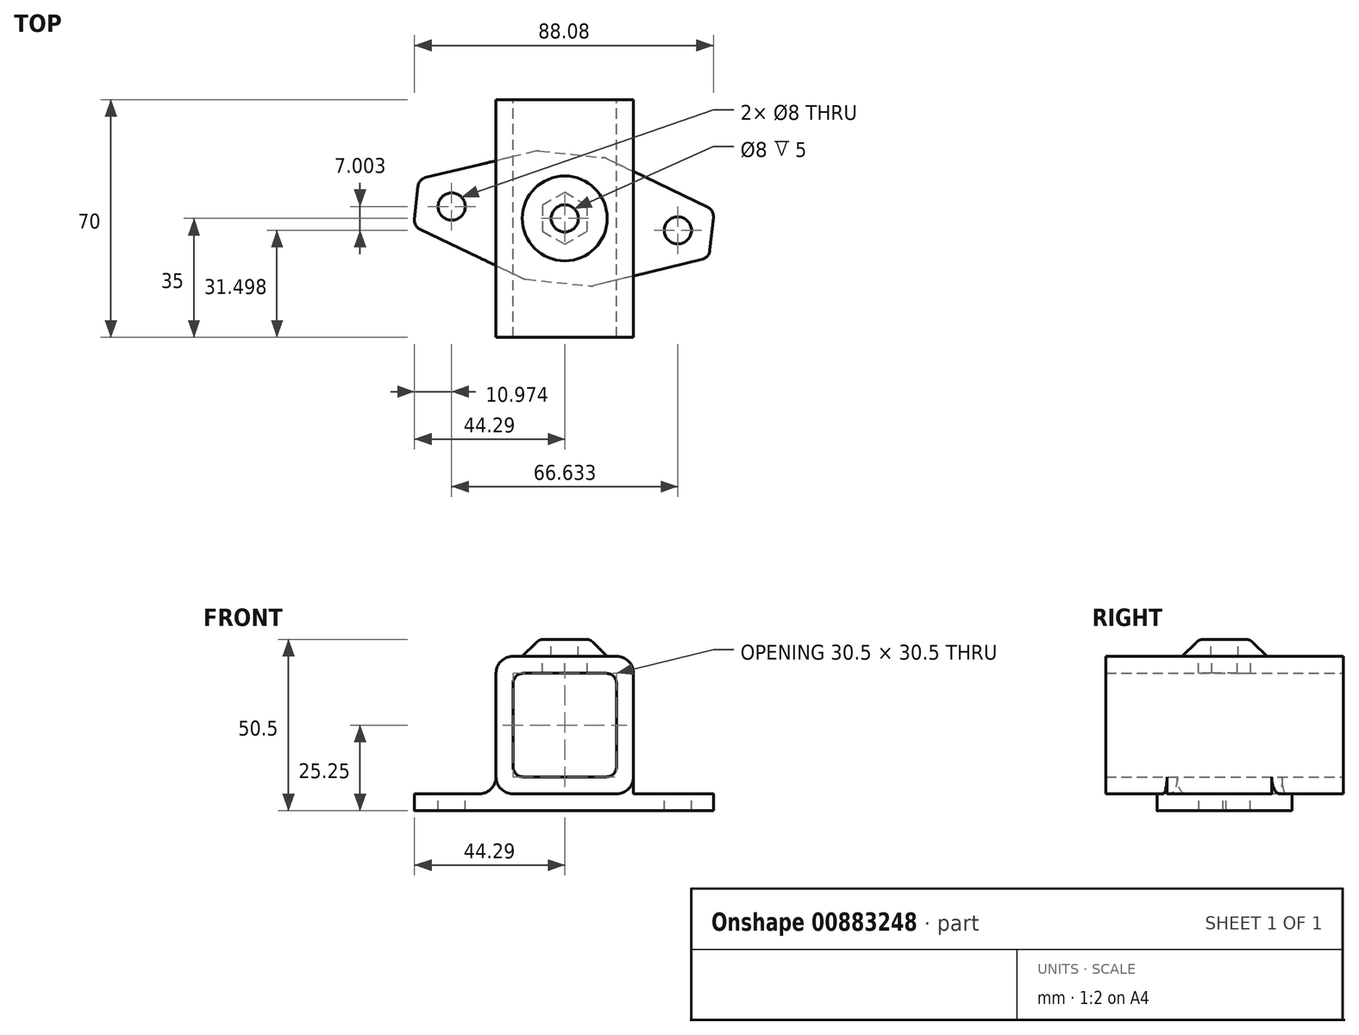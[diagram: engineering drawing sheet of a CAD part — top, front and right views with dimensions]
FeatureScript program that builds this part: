
annotation { "Feature Type Name" : "Feature", "Feature Type Description" : "" }
export const myFeature = defineFeature(function(context is Context, id is Id, definition is map)
    precondition{}
    {
        {
            var Q0;
            Q0=qCreatedBy(makeId("Front.planeOp"),FACE);
            var sketch = newSketch(context, id + "F0", { "sketchPlane" : qUnion([Q0])});
            skLineSegment(sketch, "E0.bottom", {"start": v(-12.25, -15.25) * mm, "end": v(12.25, -15.25) * mm});
            skLineSegment(sketch, "E0.top", {"start": v(-12.25, 15.25) * mm, "end": v(12.25, 15.25) * mm});
            skLineSegment(sketch, "E0.left", {"start": v(-15.25, -12.25) * mm, "end": v(-15.25, 12.25) * mm});
            skLineSegment(sketch, "E0.right", {"start": v(15.25, -12.25) * mm, "end": v(15.25, 12.25) * mm});
            skPoint(sketch, "E0.middle", {"position": v(0, 0) * mm});
            skLineSegment(sketch, "E1.0", {"start": v(-20.25, -20.25) * mm, "end": v(-20.25, 15.25) * mm});
            skLineSegment(sketch, "E1.1", {"start": v(-20.25, -20.25) * mm, "end": v(20.25, -20.25) * mm});
            skLineSegment(sketch, "E1.2", {"start": v(20.25, -20.25) * mm, "end": v(20.25, 15.25) * mm});
            skLineSegment(sketch, "E1.3", {"start": v(-15.25, 20.25) * mm, "end": v(15.25, 20.25) * mm});
            skPoint(sketch, "E2.visualSharp", {"position": v(-15.25, 15.25) * mm});
            skArc(sketch, "E2.filletArc", {"start": v(-12.25, 15.25) * mm, "mid": v(-14.37, 14.37) * mm, "end": v(-15.25, 12.25) * mm});
            skPoint(sketch, "E3.visualSharp", {"position": v(15.25, 15.25) * mm});
            skArc(sketch, "E3.filletArc", {"start": v(15.25, 12.25) * mm, "mid": v(14.37, 14.37) * mm, "end": v(12.25, 15.25) * mm});
            skPoint(sketch, "E4.visualSharp", {"position": v(15.25, -15.25) * mm});
            skArc(sketch, "E4.filletArc", {"start": v(12.25, -15.25) * mm, "mid": v(14.37, -14.37) * mm, "end": v(15.25, -12.25) * mm});
            skPoint(sketch, "E5.visualSharp", {"position": v(-15.25, -15.25) * mm});
            skArc(sketch, "E5.filletArc", {"start": v(-15.25, -12.25) * mm, "mid": v(-14.37, -14.37) * mm, "end": v(-12.25, -15.25) * mm});
            skPoint(sketch, "E6.visualSharp", {"position": v(-20.25, -20.25) * mm});
            skPoint(sketch, "E7.visualSharp", {"position": v(-20.25, 20.25) * mm});
            skArc(sketch, "E7.filletArc", {"start": v(-15.25, 20.25) * mm, "mid": v(-18.79, 18.79) * mm, "end": v(-20.25, 15.25) * mm});
            skPoint(sketch, "E8.visualSharp", {"position": v(20.25, 20.25) * mm});
            skArc(sketch, "E8.filletArc", {"start": v(20.25, 15.25) * mm, "mid": v(18.79, 18.79) * mm, "end": v(15.25, 20.25) * mm});
            skPoint(sketch, "E9.visualSharp", {"position": v(20.25, -20.25) * mm});
            skSolve(sketch);
        }
        {
            var Q0;
            Q0=makeQuery(id+"F0.imprint","IMPRINT",FACE,{"disambiguationData":[TD([[makeQuery(id+"F0.imprint","IMPRINT",EDGE,{"derivedFrom":sQuery(id+"F0.wireOp",EDGE,"E0.bottom")}),-1.0]])]});
            extrude(context, id + "F1", {"entities" : qUnion([Q0]), "endBound" : BoundingType.SYMMETRIC, "depth" : 70 * mm, "offsetDistance" : 25 * mm});
        }
        {
            var Q0;
            Q0=makeQuery(id+"F1.opExtrude","SWEPT_FACE",FACE,{"disambiguationData":[OSD([sQuery(id+"F0.wireOp",EDGE,"E1.3")])]});
            var sketch = newSketch(context, id + "F2", { "sketchPlane" : qUnion([Q0])});
            skCircle(sketch, "E10.cCircle", {"center": v(0, 0) * mm, "radius": 6.6 * mm, "construction": true});
            skLineSegment(sketch, "E10.0", {"start": v(6.6, 3.81) * mm, "end": v(6.6, -3.81) * mm});
            skLineSegment(sketch, "E10.1", {"start": v(6.6, -3.81) * mm, "end": v(0, -7.62) * mm});
            skLineSegment(sketch, "E10.2", {"start": v(0, -7.62) * mm, "end": v(-6.6, -3.81) * mm});
            skLineSegment(sketch, "E10.3", {"start": v(-6.6, -3.81) * mm, "end": v(-6.6, 3.81) * mm});
            skLineSegment(sketch, "E10.4", {"start": v(-6.6, 3.81) * mm, "end": v(0, 7.62) * mm});
            skLineSegment(sketch, "E10.5", {"start": v(0, 7.62) * mm, "end": v(6.6, 3.81) * mm});
            skPoint(sketch, "E10.0.midPoint", {"position": v(6.6, 0) * mm});
            skSolve(sketch);
        }
        {
            var Q0;
            Q0 = qSketchRegion(id + "F2", true);
            extrude(context, id + "F3", {"entities" : qUnion([Q0]), "operationType" : NewBodyOperationType.REMOVE, "endBound" : BoundingType.UP_TO_NEXT, "oppositeDirection" : true, "depth" : 25 * mm, "offsetDistance" : 25 * mm});
        }
        {
            var Q0;
            Q0=makeQuery(id+"F1.opExtrude","SWEPT_FACE",FACE,{"disambiguationData":[OSD([sQuery(id+"F0.wireOp",EDGE,"E1.3")])]});
            var sketch = newSketch(context, id + "F4", { "sketchPlane" : qUnion([Q0])});
            skCircle(sketch, "E11", {"center": v(0, 0) * mm, "radius": 12.5 * mm});
            skSolve(sketch);
        }
        {
            var Q0;
            Q0=makeQuery(id+"F4.imprint","IMPRINT",FACE,{"disambiguationData":[TD([[makeQuery(id+"F4.imprint","IMPRINT",EDGE,{"derivedFrom":sQuery(id+"F4.wireOp",EDGE,"E11")}),-1.0]])]});
            cPlane(context, id + "F5", {"entities" : qUnion([Q0]), "cplaneType" : CPlaneType.OFFSET, "offset" : 5 * mm, "width" : 150 * mm, "height" : 150 * mm});
        }
        {
            var Q0;
            Q0=qCreatedBy(id+"F5.planeOp",FACE);
            var sketch = newSketch(context, id + "F6", { "sketchPlane" : qUnion([Q0])});
            skCircle(sketch, "E12", {"center": v(0, 0) * mm, "radius": 7.5 * mm});
            skSolve(sketch);
        }
        {
            var Q0;
            Q0=makeQuery(id+"F1.opExtrude","SWEPT_FACE",FACE,{"disambiguationData":[OSD([sQuery(id+"F0.wireOp",EDGE,"E1.3")])]});
            cPlane(context, id + "F7", {"entities" : qUnion([Q0]), "cplaneType" : CPlaneType.OFFSET, "offset" : 0 * mm, "width" : 150 * mm, "height" : 150 * mm});
        }
        {
            var Q0;
            Q0=qCreatedBy(id+"F7.planeOp",FACE);
            var sketch = newSketch(context, id + "F8", { "sketchPlane" : qUnion([Q0])});
            skCircle(sketch, "E13", {"center": v(0, 0) * mm, "radius": 12.5 * mm});
            skSolve(sketch);
        }
        {
            var Q1;
            Q1 = qSketchRegion(id + "F8", true);
            var Q2;
            Q2 = qSketchRegion(id + "F6", true);
            loft(context, id + "F9", {"operationType" : NewBodyOperationType.ADD, "sheetProfilesArray" : [{ "sheetProfileEntities" : qUnion([Q1]) }, { "sheetProfileEntities" : qUnion([Q2]) }]});
        }
        {
            var Q0;
            Q0=makeQuery(id+"F9.opLoft","MID_CAP_EDGE",EDGE,{"disambiguationData":[OSD([sQuery(id+"F8.wireOp",EDGE,"E13")])],"capPos":0.0});
            var Q1;
            Q1=makeQuery(id+"F9.opLoft","MID_CAP_EDGE",EDGE,{"disambiguationData":[OSD([sQuery(id+"F6.wireOp",EDGE,"E12")])],"capPos":1.0});
            fillet(context, id + "F10", {"entities" : qUnion([Q0, Q1]), "radius" : 3 * mm, "tangentPropagation" : true, "allowEdgeOverflow" : false});
        }
        {
            var Q0;
            Q0=makeQuery(id+"F6.imprint","IMPRINT",FACE,{"disambiguationData":[TD([[makeQuery(id+"F6.imprint","IMPRINT",EDGE,{"derivedFrom":sQuery(id+"F6.wireOp",EDGE,"E12")}),1.0]])]});
            var sketch = newSketch(context, id + "F11", { "sketchPlane" : qUnion([Q0])});
            skCircle(sketch, "E14", {"center": v(0, 0) * mm, "radius": 4 * mm});
            skSolve(sketch);
        }
        {
            var Q0;
            Q0 = qSketchRegion(id + "F11", true);
            extrude(context, id + "F12", {"entities" : qUnion([Q0]), "operationType" : NewBodyOperationType.REMOVE, "endBound" : BoundingType.UP_TO_NEXT, "oppositeDirection" : true, "depth" : 25 * mm, "offsetDistance" : 25 * mm});
        }
        {
            var Q0;
            Q0=makeQuery(id+"F1.opExtrude","SWEPT_FACE",FACE,{"disambiguationData":[OSD([sQuery(id+"F0.wireOp",EDGE,"E1.1")])]});
            var sketch = newSketch(context, id + "F13", { "sketchPlane" : qUnion([Q0])});
            skLineSegment(sketch, "E15", {"start": v(-33.32, -3.5) * mm, "end": v(33.32, 3.5) * mm, "construction": true});
            skLineSegment(sketch, "E16", {"start": v(0, 0) * mm, "end": v(70.81, 0) * mm, "construction": true});
            skPoint(sketch, "E16.endSnap0", {"position": v(-20.25, 0) * mm});
            skCircle(sketch, "E17", {"center": v(33.32, 3.5) * mm, "radius": 4 * mm});
            skCircle(sketch, "E18", {"center": v(-33.32, -3.5) * mm, "radius": 4 * mm});
            skLineSegment(sketch, "E19", {"start": v(-33.32, -3.5) * mm, "end": v(-43.76, -4.6) * mm, "construction": true});
            skLineSegment(sketch, "E20", {"start": v(-43.76, -4.6) * mm, "end": v(-44.5, 2.36) * mm});
            skLineSegment(sketch, "E21", {"start": v(-44.5, 2.36) * mm, "end": v(-11.93, 17.85) * mm});
            skLineSegment(sketch, "E22", {"start": v(-11.93, 17.85) * mm, "end": v(7.96, 19.94) * mm});
            skLineSegment(sketch, "E23", {"start": v(0, 0) * mm, "end": v(-1.99, 18.9) * mm, "construction": true});
            skLineSegment(sketch, "E24", {"start": v(33.32, 3.5) * mm, "end": v(43.26, 4.55) * mm, "construction": true});
            skLineSegment(sketch, "E25", {"start": v(43.26, 4.55) * mm, "end": v(42.53, 11.5) * mm});
            skLineSegment(sketch, "E26", {"start": v(42.53, 11.5) * mm, "end": v(7.96, 19.94) * mm});
            skLineSegment(sketch, "E27", {"start": v(43.26, 4.55) * mm, "end": v(44, -2.41) * mm});
            skLineSegment(sketch, "E28", {"start": v(-43.76, -4.6) * mm, "end": v(-43.03, -11.56) * mm});
            skLineSegment(sketch, "E29", {"start": v(0, 0) * mm, "end": v(1.99, -18.9) * mm, "construction": true});
            skLineSegment(sketch, "E30", {"start": v(-7.96, -19.94) * mm, "end": v(11.93, -17.85) * mm});
            skLineSegment(sketch, "E31", {"start": v(-7.96, -19.94) * mm, "end": v(-43.03, -11.56) * mm});
            skLineSegment(sketch, "E32", {"start": v(11.93, -17.85) * mm, "end": v(44, -2.41) * mm});
            skSolve(sketch);
        }
        {
            var Q0;
            Q0 = qSketchRegion(id + "F13", true);
            extrude(context, id + "F14", {"entities" : qUnion([Q0]), "operationType" : NewBodyOperationType.ADD, "depth" : 5 * mm, "offsetDistance" : 25 * mm});
        }
        {
            var Q0;
            Q0=makeQuery(id+"F14.opExtrude","SWEPT_EDGE",EDGE,{"disambiguationData":[OSD([sQuery(id+"F13.wireOp",EDGE,"E25"),sQuery(id+"F13.wireOp",EDGE,"E26")])]});
            var Q1;
            Q1=makeQuery(id+"F14.opExtrude","SWEPT_EDGE",EDGE,{"disambiguationData":[OSD([sQuery(id+"F13.wireOp",EDGE,"E22"),sQuery(id+"F13.wireOp",EDGE,"E26")])]});
            var Q2;
            Q2=makeQuery(id+"F14.opExtrude","SWEPT_EDGE",EDGE,{"disambiguationData":[OSD([sQuery(id+"F13.wireOp",EDGE,"E21"),sQuery(id+"F13.wireOp",EDGE,"E22")])]});
            var Q3;
            Q3=makeQuery(id+"F14.opExtrude","SWEPT_EDGE",EDGE,{"disambiguationData":[OSD([sQuery(id+"F13.wireOp",EDGE,"E20"),sQuery(id+"F13.wireOp",EDGE,"E21")])]});
            var Q4;
            Q4=makeQuery(id+"F14.opExtrude","SWEPT_EDGE",EDGE,{"disambiguationData":[OSD([sQuery(id+"F13.wireOp",EDGE,"E28"),sQuery(id+"F13.wireOp",EDGE,"E31")])]});
            var Q5;
            Q5=makeQuery(id+"F14.opExtrude","SWEPT_EDGE",EDGE,{"disambiguationData":[OSD([sQuery(id+"F13.wireOp",EDGE,"E30"),sQuery(id+"F13.wireOp",EDGE,"E31")])]});
            var Q6;
            Q6=makeQuery(id+"F14.opExtrude","SWEPT_EDGE",EDGE,{"disambiguationData":[OSD([sQuery(id+"F13.wireOp",EDGE,"E30"),sQuery(id+"F13.wireOp",EDGE,"E32")])]});
            var Q7;
            Q7=makeQuery(id+"F14.opExtrude","SWEPT_EDGE",EDGE,{"disambiguationData":[OSD([sQuery(id+"F13.wireOp",EDGE,"E27"),sQuery(id+"F13.wireOp",EDGE,"E32")])]});
            fillet(context, id + "F15", {"entities" : qUnion([Q0, Q1, Q2, Q3, Q4, Q5, Q6, Q7]), "radius" : 3 * mm, "tangentPropagation" : true, "allowEdgeOverflow" : false});
        }
        {
            var Q0;
            {var subQ0=sQuery(id+"F13.wireOp",EDGE,"E31");var subQ1=sQuery(id+"F0.wireOp",EDGE,"E1.1");var subQ2=sQuery(id+"F0.wireOp",EDGE,"E1.0");var subQ3=makeQuery(id+"F1.opExtrude","SWEPT_FACE",FACE,{"disambiguationData":[OSD([subQ1])]});var subQ4=makeQuery(id+"F1.opExtrude","SWEPT_FACE",FACE,{"disambiguationData":[OSD([subQ2])]});Q0=makeQuery(id+"F14.boolean.opBoolean","SPLIT",EDGE,{"disambiguationData":[topologyDisambiguationEdgeConnected([subQ4,subQ3]),TD([makeQuery(id+"F14.opExtrude","SWEPT_FACE",FACE,{"disambiguationData":[OSD([subQ0])]})])],"derivedFrom":makeQuery(id+"F1.opExtrude","SWEPT_EDGE",EDGE,{"disambiguationData":[OSD([subQ2,subQ1])]})});}
            var Q1;
            {var subQ0=sQuery(id+"F13.wireOp",EDGE,"E32");var subQ1=sQuery(id+"F0.wireOp",EDGE,"E1.2");var subQ2=sQuery(id+"F0.wireOp",EDGE,"E1.1");var subQ3=makeQuery(id+"F1.opExtrude","SWEPT_FACE",FACE,{"disambiguationData":[OSD([subQ1])]});var subQ4=makeQuery(id+"F1.opExtrude","SWEPT_FACE",FACE,{"disambiguationData":[OSD([subQ2])]});Q1=makeQuery(id+"F14.boolean.opBoolean","SPLIT",EDGE,{"disambiguationData":[topologyDisambiguationEdgeConnected([subQ4,subQ3]),TD([makeQuery(id+"F14.opExtrude","SWEPT_FACE",FACE,{"disambiguationData":[OSD([subQ0])]})])],"derivedFrom":makeQuery(id+"F1.opExtrude","SWEPT_EDGE",EDGE,{"disambiguationData":[OSD([subQ2,subQ1])]})});}
            var Q2;
            {var subQ0=sQuery(id+"F13.wireOp",EDGE,"E21");var subQ1=sQuery(id+"F0.wireOp",EDGE,"E1.0");var subQ2=makeQuery(id+"F1.opExtrude","SWEPT_FACE",FACE,{"disambiguationData":[OSD([subQ1])]});var subQ3=sQuery(id+"F0.wireOp",EDGE,"E1.1");var subQ4=makeQuery(id+"F1.opExtrude","SWEPT_FACE",FACE,{"disambiguationData":[OSD([subQ3])]});Q2=makeQuery(id+"F14.boolean.opBoolean","SPLIT",EDGE,{"disambiguationData":[topologyDisambiguationEdgeConnected([subQ2,subQ4]),TD([makeQuery(id+"F14.opExtrude","SWEPT_FACE",FACE,{"disambiguationData":[OSD([subQ0])]})])],"derivedFrom":makeQuery(id+"F1.opExtrude","SWEPT_EDGE",EDGE,{"disambiguationData":[OSD([subQ1,subQ3])]})});}
            var Q3;
            {var subQ0=sQuery(id+"F13.wireOp",EDGE,"E26");var subQ1=sQuery(id+"F0.wireOp",EDGE,"E1.2");var subQ2=makeQuery(id+"F1.opExtrude","SWEPT_FACE",FACE,{"disambiguationData":[OSD([subQ1])]});var subQ3=sQuery(id+"F0.wireOp",EDGE,"E1.1");var subQ4=makeQuery(id+"F1.opExtrude","SWEPT_FACE",FACE,{"disambiguationData":[OSD([subQ3])]});Q3=makeQuery(id+"F14.boolean.opBoolean","SPLIT",EDGE,{"disambiguationData":[topologyDisambiguationEdgeConnected([subQ4,subQ2]),TD([makeQuery(id+"F14.opExtrude","SWEPT_FACE",FACE,{"disambiguationData":[OSD([subQ0])]})])],"derivedFrom":makeQuery(id+"F1.opExtrude","SWEPT_EDGE",EDGE,{"disambiguationData":[OSD([subQ3,subQ1])]})});}
            fillet(context, id + "F16", {"entities" : qUnion([Q0, Q1, Q2, Q3]), "radius" : 5 * mm, "tangentPropagation" : true, "allowEdgeOverflow" : false});
        }
        {
            var Q0;
            {var subQ0=sQuery(id+"F0.wireOp",EDGE,"E1.0");Q0=makeQuery(id+"F14.boolean.opBoolean","SPLIT",EDGE,{"disambiguationData":[topologyDisambiguationEdgeConnected([makeQuery(id+"F1.opExtrude","SWEPT_FACE",FACE,{"disambiguationData":[OSD([subQ0])]}),makeQuery(id+"F14.opExtrude","CAP_FACE",FACE,{"disambiguationData":[OSD([sQuery(id+"F13.wireOp",EDGE,"E17"),sQuery(id+"F13.wireOp",EDGE,"E18"),sQuery(id+"F13.wireOp",EDGE,"E20"),sQuery(id+"F13.wireOp",EDGE,"E21"),sQuery(id+"F13.wireOp",EDGE,"E22"),sQuery(id+"F13.wireOp",EDGE,"E25"),sQuery(id+"F13.wireOp",EDGE,"E26"),sQuery(id+"F13.wireOp",EDGE,"E27"),sQuery(id+"F13.wireOp",EDGE,"E28"),sQuery(id+"F13.wireOp",EDGE,"E30"),sQuery(id+"F13.wireOp",EDGE,"E31"),sQuery(id+"F13.wireOp",EDGE,"E32")])],"isStart":true})])],"derivedFrom":makeQuery(id+"F1.opExtrude","SWEPT_EDGE",EDGE,{"disambiguationData":[OSD([subQ0,sQuery(id+"F0.wireOp",EDGE,"E1.1")])]})});}
            var Q1;
            {var subQ0=sQuery(id+"F0.wireOp",EDGE,"E1.2");Q1=makeQuery(id+"F14.boolean.opBoolean","SPLIT",EDGE,{"disambiguationData":[topologyDisambiguationEdgeConnected([makeQuery(id+"F1.opExtrude","SWEPT_FACE",FACE,{"disambiguationData":[OSD([subQ0])]}),makeQuery(id+"F14.opExtrude","CAP_FACE",FACE,{"disambiguationData":[OSD([sQuery(id+"F13.wireOp",EDGE,"E17"),sQuery(id+"F13.wireOp",EDGE,"E18"),sQuery(id+"F13.wireOp",EDGE,"E20"),sQuery(id+"F13.wireOp",EDGE,"E21"),sQuery(id+"F13.wireOp",EDGE,"E22"),sQuery(id+"F13.wireOp",EDGE,"E25"),sQuery(id+"F13.wireOp",EDGE,"E26"),sQuery(id+"F13.wireOp",EDGE,"E27"),sQuery(id+"F13.wireOp",EDGE,"E28"),sQuery(id+"F13.wireOp",EDGE,"E30"),sQuery(id+"F13.wireOp",EDGE,"E31"),sQuery(id+"F13.wireOp",EDGE,"E32")])],"isStart":true})])],"derivedFrom":makeQuery(id+"F1.opExtrude","SWEPT_EDGE",EDGE,{"disambiguationData":[OSD([sQuery(id+"F0.wireOp",EDGE,"E1.1"),subQ0])]})});}
            fillet(context, id + "F17", {"entities" : qUnion([Q0, Q1]), "radius" : 5 * mm, "tangentPropagation" : true, "allowEdgeOverflow" : false});
        }
    });
